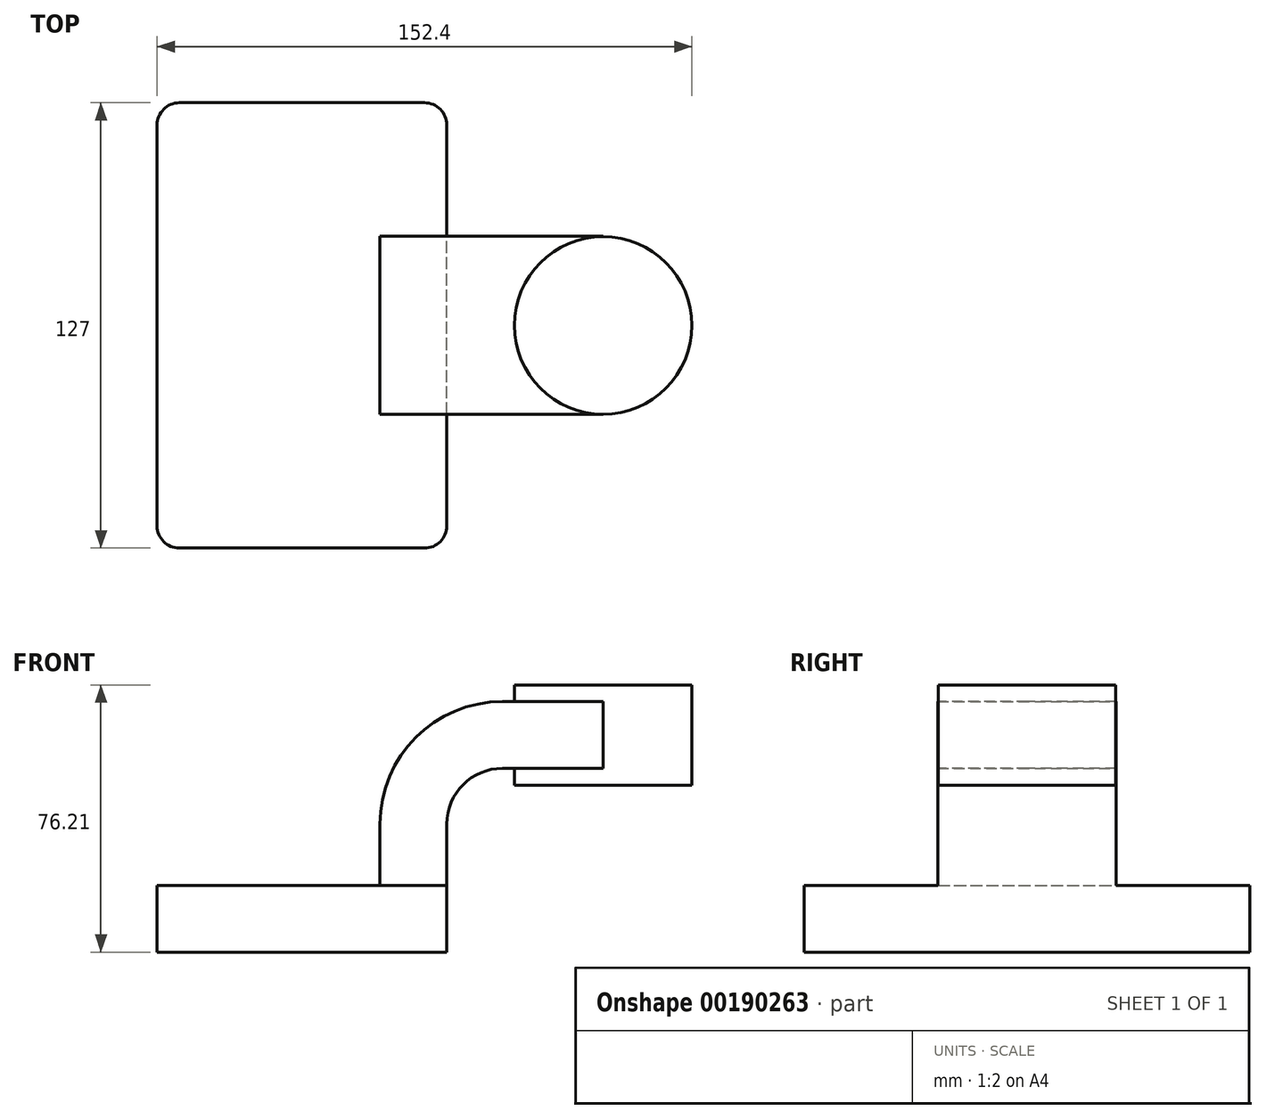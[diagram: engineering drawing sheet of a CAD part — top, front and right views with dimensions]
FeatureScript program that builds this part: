
annotation { "Feature Type Name" : "Feature", "Feature Type Description" : "" }
export const myFeature = defineFeature(function(context is Context, id is Id, definition is map)
    precondition{}
    {
        {
            var Q0;
            Q0=qCreatedBy(makeId("Front.planeOp"),FACE);
            var sketch = newSketch(context, id + "F0", { "sketchPlane" : qUnion([Q0])});
            skLineSegment(sketch, "E0.bottom", {"start": v(41.28, -9.52) * mm, "end": v(-41.28, -9.53) * mm});
            skLineSegment(sketch, "E0.top", {"start": v(41.28, 9.53) * mm, "end": v(-41.28, 9.52) * mm});
            skLineSegment(sketch, "E0.left", {"start": v(41.28, -9.52) * mm, "end": v(41.28, 9.53) * mm});
            skLineSegment(sketch, "E0.right", {"start": v(-41.28, -9.53) * mm, "end": v(-41.28, 9.52) * mm});
            skPoint(sketch, "E0.middle", {"position": v(0, 0) * mm});
            skLineSegment(sketch, "E1.bottom", {"start": v(111.12, 38.1) * mm, "end": v(60.32, 38.1) * mm});
            skLineSegment(sketch, "E1.top", {"start": v(111.12, 66.68) * mm, "end": v(60.32, 66.68) * mm});
            skLineSegment(sketch, "E1.left", {"start": v(111.12, 38.1) * mm, "end": v(111.12, 66.68) * mm});
            skLineSegment(sketch, "E1.right", {"start": v(60.32, 38.1) * mm, "end": v(60.32, 66.68) * mm});
            skPoint(sketch, "E1.middle", {"position": v(85.72, 52.39) * mm});
            skLineSegment(sketch, "E2", {"start": v(41.28, 9.53) * mm, "end": v(41.28, 27) * mm});
            skArc(sketch, "E3", {"start": v(41.28, 27) * mm, "mid": v(45.92, 38.23) * mm, "end": v(57.15, 42.88) * mm});
            skLineSegment(sketch, "E4", {"start": v(57.15, 42.88) * mm, "end": v(85.82, 42.88) * mm});
            skLineSegment(sketch, "E5.0", {"start": v(57.15, 61.93) * mm, "end": v(85.82, 61.93) * mm});
            skArc(sketch, "E5.1", {"start": v(22.23, 27) * mm, "mid": v(32.45, 51.7) * mm, "end": v(57.15, 61.93) * mm});
            skLineSegment(sketch, "E5.2", {"start": v(22.23, 9.53) * mm, "end": v(22.23, 27) * mm});
            skFitSpline(sketch, "E6", {"points": [v(-41.28, 9.53) * mm, v(57.15, 61.93) * mm], "startDerivative": vector(0.37, 70.47) * mm, "endDerivative": vector(118.75, -0.76) * mm});
            skLineSegment(sketch, "E7", {"start": v(85.82, 38.1) * mm, "end": v(85.82, 66.68) * mm});
            skSolve(sketch);
        }
        {
            var Q0;
            Q0=makeQuery(id+"F0.imprint","IMPRINT",FACE,{"disambiguationData":[TD([[makeQuery(id+"F0.imprint","IMPRINT",EDGE,{"derivedFrom":sQuery(id+"F0.wireOp",EDGE,"E0.bottom")}),-1.0]])]});
            extrude(context, id + "F1", {"entities" : qUnion([Q0]), "endBound" : BoundingType.SYMMETRIC, "depth" : 127 * mm});
        }
        {
            var Q0;
            {var subQ1=sQuery(id+"F0.wireOp",EDGE,"E2");Q0=makeQuery(id+"F0.imprint","IMPRINT",FACE,{"disambiguationData":[TD([[makeQuery(id+"F0.imprint","IMPRINT",EDGE,{"derivedFrom":subQ1}),1.0]])]});}
            var Q1;
            {var subQ0=sQuery(id+"F0.wireOp",EDGE,"E4");var subQ1=sQuery(id+"F0.wireOp",EDGE,"E1.right");var subQ2=makeQuery(id+"F0.imprint","INTERSECT",VERTEX,{"derivedFrom":[subQ1,subQ0]});Q1=makeQuery(id+"F0.imprint","IMPRINT",FACE,{"disambiguationData":[TD([[makeQuery(id+"F0.imprint","IMPRINT",EDGE,{"disambiguationData":[TD([[subQ2,-1.0]])],"derivedFrom":subQ1}),-1.0]])]});}
            extrude(context, id + "F2", {"entities" : qUnion([Q0, Q1]), "operationType" : NewBodyOperationType.ADD, "endBound" : BoundingType.SYMMETRIC, "depth" : 50.8 * mm});
        }
        {
            var Q0;
            Q0=makeQuery(id+"F0.imprint","IMPRINT",FACE,{"disambiguationData":[TD([[makeQuery(id+"F0.imprint","IMPRINT",EDGE,{"derivedFrom":sQuery(id+"F0.wireOp",EDGE,"E5.1")}),1.0]])]});
            extrude(context, id + "F3", {"entities" : qUnion([Q0]), "operationType" : NewBodyOperationType.ADD, "endBound" : BoundingType.SYMMETRIC, "depth" : 15.88 * mm});
        }
        {
            var Q0;
            Q0=makeQuery(id+"F0.imprint","IMPRINT",FACE,{"disambiguationData":[TD([[makeQuery(id+"F0.imprint","IMPRINT",EDGE,{"derivedFrom":sQuery(id+"F0.wireOp",EDGE,"E0.bottom")}),-1.0]])]});
            extrude(context, id + "F4", {"entities" : qUnion([Q0]), "operationType" : NewBodyOperationType.ADD, "depth" : 25.4 * mm});
        }
        {
            var Q0;
            {var subQ0=sQuery(id+"F0.wireOp",EDGE,"E1.left");Q0=makeQuery(id+"F0.imprint","IMPRINT",FACE,{"disambiguationData":[TD([[makeQuery(id+"F0.imprint","IMPRINT",EDGE,{"derivedFrom":subQ0}),1.0]])]});}
            var Q1;
            Q1=sQuery(id+"F0.wireOp",EDGE,"E7");
            revolve(context, id + "F5", {"operationType" : NewBodyOperationType.ADD, "entities" : qUnion([Q0]), "axis" : qUnion([Q1]), "revolveType" : RevolveType.FULL});
        }
        {
            var Q0;
            Q0=makeQuery(id+"F1.opExtrude","CAP_EDGE",EDGE,{"disambiguationData":[OSD([sQuery(id+"F0.wireOp",EDGE,"E0.right")])],"isStart":false});
            var Q1;
            Q1=makeQuery(id+"F1.opExtrude","CAP_EDGE",EDGE,{"disambiguationData":[OSD([sQuery(id+"F0.wireOp",EDGE,"E0.left")])],"isStart":false});
            var Q2;
            Q2=makeQuery(id+"F1.opExtrude","CAP_EDGE",EDGE,{"disambiguationData":[OSD([sQuery(id+"F0.wireOp",EDGE,"E0.right")])],"isStart":true});
            var Q3;
            Q3=makeQuery(id+"F1.opExtrude","CAP_EDGE",EDGE,{"disambiguationData":[OSD([sQuery(id+"F0.wireOp",EDGE,"E0.left")])],"isStart":true});
            fillet(context, id + "F6", {"entities" : qUnion([Q0, Q1, Q2, Q3]), "radius" : 6.35 * mm, "tangentPropagation" : true, "allowEdgeOverflow" : false});
        }
    });
